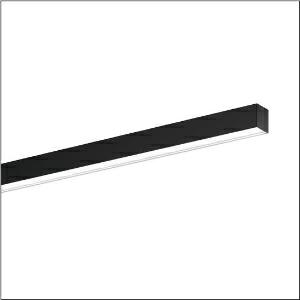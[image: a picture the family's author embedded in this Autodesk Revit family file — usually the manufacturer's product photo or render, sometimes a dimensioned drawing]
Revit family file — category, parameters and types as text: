
# Revit family: silica_r__21_51mx20da32bb_5abe
name_source: partatom
category: Lighting Fixtures
units: mm (PartAtom-declared; Revit-internal decimal feet)

## family parameters
Cut with Voids When Loaded = No
Host = Face
Light Source = No
Part Type = Normal
Room Calculation Point = No
Round Connector Dimension = Use Diameter
Shared = No

## types (1)
- --- (1 x LED, 2400 lm, 16.1 W, 3000K)
    Apparent Load = 16 VA
    CIE Flux Codes = 48 79 96 100 100
    Color Rendering = 80
    Color Temperature = 3000K
    Default Elevation = 1800 mm
    Description = Silica® 21, office luminaire, primary optical cover: cover, of PMMA, opal, light emission: direct distribution, primary light characteristic: symmetric, installation type: surface-mounted, LED, rated luminous flux: 2.400lm, luminous efficacy: 149lm/W, light colour: 830, colour temperature: 3000K, with terminal, 3+2-pole, max. 2.5mm², mains connection: 220..240V, AC, 50/60Hz, rated input power: 16.1W, luminaire housing, of aluminium, jet black (RAL 9005), length: 1.204mm, width: 53mm, height: 53mm, protection rating (complete): IP20, insulation class (complete): insulation class I (protective earthing), certification: CE, permissible operating ambient temperature: 0..+35°C, standard: EN 50419, packaging unit: 1 piece
    Height = 0 mm  [stored 0 ft]
    Lamp = 1 x LED
    Lamp Light Flux = 2400 lm
    Lamp Power = 16.1 W
    Lamp count = 1
    Length = 1204 mm
    Luminous efficacy = 149 lm/W
    Manufacturer = Siteco
    ModVariant = No
    Model = 51MX20DA32BB
    Mounting Place = Ceiling
    Mounting Type = Recessed
    Number of Poles = 1
    OnlyDefault = Yes
    Power Factor = 1
    Product Name = Silica® 21
    Product group = office luminaire | ceiling recessed
    ProductGroupID = 401
    Protection Class = Protection class I
    Protection Degree = IP 20
    RLX_Detail_Level = 1
    RLX_Emergency_Light_Flux = 0 lm
    RLX_Emergency_Type = 0
    RLX_Emergency_Type_DB = No
    RlxData = <blob elided: 28761 chars, md5=d00fbf06>
    Socket = socket
    Standby Power = 0 W
    System Light Flux = 2400 lm
    System Power = 16 W
    Type Comments = factory setting: luminous flux: 100 % | dim-lin: 254 | 233 mA
    Type Image = l_1297760.jpg
    URL = http://relux.com
    VarID = @adj_048329
    Voltage = 0 V
    Weight = 0.00 kg
    Width = 53 mm

note: [stored X ft] marks values corroborated as IEEE doubles in the binary element streams (Revit-internal decimal feet)

## geometry (parser evidence)
native form markers: Blend x4, Sweep x10
no freeform markers — native parametric forms only
